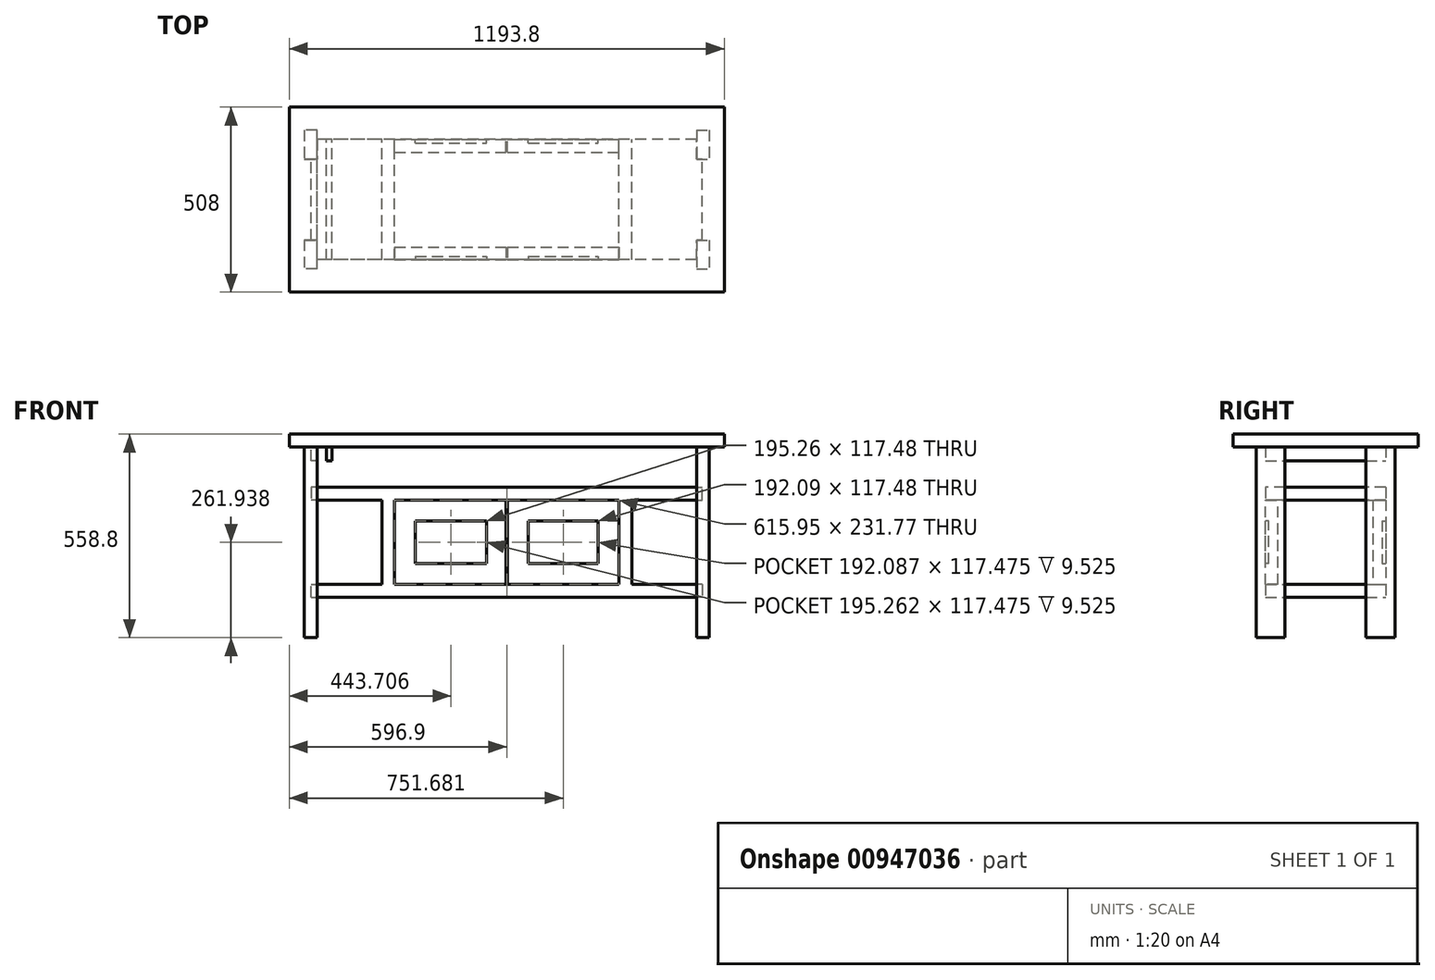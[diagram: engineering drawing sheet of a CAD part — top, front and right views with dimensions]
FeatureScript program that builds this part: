
annotation { "Feature Type Name" : "Feature", "Feature Type Description" : "" }
export const myFeature = defineFeature(function(context is Context, id is Id, definition is map)
    precondition{}
    {
        {
            var Q0;
            Q0=qCreatedBy(makeId("Front.planeOp"),FACE);
            var sketch = newSketch(context, id + "F0", { "sketchPlane" : qUnion([Q0])});
            skLineSegment(sketch, "E0.bottom", {"start": v(596.9, 558.8) * mm, "end": v(-596.9, 558.8) * mm});
            skLineSegment(sketch, "E0.top", {"start": v(596.9, 523.88) * mm, "end": v(-596.9, 523.88) * mm});
            skLineSegment(sketch, "E0.left", {"start": v(596.9, 558.8) * mm, "end": v(596.9, 523.88) * mm});
            skLineSegment(sketch, "E0.right", {"start": v(-596.9, 558.8) * mm, "end": v(-596.9, 523.88) * mm});
            skPoint(sketch, "E0.middle", {"position": v(0, 541.34) * mm});
            skLineSegment(sketch, "E1.bottom", {"start": v(536.58, 146.05) * mm, "end": v(342.9, 146.05) * mm});
            skLineSegment(sketch, "E1.top", {"start": v(536.58, 111.13) * mm, "end": v(-536.58, 111.12) * mm});
            skLineSegment(sketch, "E1.left", {"start": v(536.58, 146.05) * mm, "end": v(536.58, 111.13) * mm});
            skLineSegment(sketch, "E1.right", {"start": v(-536.58, 146.05) * mm, "end": v(-536.58, 111.12) * mm});
            skPoint(sketch, "E1.middle", {"position": v(0, 128.59) * mm});
            skLineSegment(sketch, "E2", {"start": v(307.98, 146.05) * mm, "end": v(307.98, 377.83) * mm});
            skLineSegment(sketch, "E3", {"start": v(342.9, 377.82) * mm, "end": v(342.9, 146.05) * mm});
            skLineSegment(sketch, "E4", {"start": v(0, 0) * mm, "end": v(0, -191.79) * mm, "construction": true});
            skLineSegment(sketch, "E5.MirrorCS", {"start": v(-342.9, 377.82) * mm, "end": v(-342.9, 146.05) * mm});
            skLineSegment(sketch, "E6.MirrorCS", {"start": v(-307.98, 146.05) * mm, "end": v(-307.98, 377.83) * mm});
            skLineSegment(sketch, "E7.trimOffspring", {"start": v(307.98, 146.05) * mm, "end": v(-307.98, 146.05) * mm});
            skLineSegment(sketch, "E8.trimOffspring", {"start": v(-342.9, 146.05) * mm, "end": v(-536.58, 146.05) * mm});
            skLineSegment(sketch, "E9.bottom", {"start": v(-536.58, 377.83) * mm, "end": v(-342.9, 377.83) * mm});
            skLineSegment(sketch, "E9.top", {"start": v(-536.58, 412.75) * mm, "end": v(536.57, 412.75) * mm});
            skLineSegment(sketch, "E9.left", {"start": v(-536.58, 377.83) * mm, "end": v(-536.58, 412.75) * mm});
            skLineSegment(sketch, "E9.right", {"start": v(536.58, 377.83) * mm, "end": v(536.58, 412.75) * mm});
            skLineSegment(sketch, "E10.trimOffspring", {"start": v(-307.98, 377.83) * mm, "end": v(307.97, 377.83) * mm});
            skLineSegment(sketch, "E11.trimOffspring", {"start": v(342.9, 377.83) * mm, "end": v(536.57, 377.83) * mm});
            skLineSegment(sketch, "E12", {"start": v(-342.9, 377.83) * mm, "end": v(-307.98, 377.83) * mm, "construction": true});
            skLineSegment(sketch, "E13.bottom", {"start": v(536.57, 523.88) * mm, "end": v(520.7, 523.88) * mm});
            skLineSegment(sketch, "E13.top", {"start": v(536.57, 485.78) * mm, "end": v(520.7, 485.78) * mm});
            skLineSegment(sketch, "E13.left", {"start": v(536.57, 523.88) * mm, "end": v(536.57, 485.78) * mm});
            skLineSegment(sketch, "E13.right", {"start": v(520.7, 523.88) * mm, "end": v(520.7, 485.78) * mm});
            skLineSegment(sketch, "E14.bottom", {"start": v(495.3, 523.88) * mm, "end": v(479.43, 523.88) * mm});
            skLineSegment(sketch, "E14.top", {"start": v(495.3, 485.78) * mm, "end": v(479.43, 485.78) * mm});
            skLineSegment(sketch, "E14.left", {"start": v(495.3, 523.88) * mm, "end": v(495.3, 485.78) * mm});
            skLineSegment(sketch, "E14.right", {"start": v(479.43, 523.88) * mm, "end": v(479.43, 485.78) * mm});
            skLineSegment(sketch, "E15.MirrorCS", {"start": v(-520.7, 523.88) * mm, "end": v(-520.7, 485.77) * mm});
            skLineSegment(sketch, "E16.MirrorCS", {"start": v(-495.3, 485.78) * mm, "end": v(-479.43, 485.78) * mm});
            skLineSegment(sketch, "E17.MirrorCS", {"start": v(-536.58, 485.77) * mm, "end": v(-520.7, 485.77) * mm});
            skLineSegment(sketch, "E18.MirrorCS", {"start": v(-495.3, 523.88) * mm, "end": v(-495.3, 485.77) * mm});
            skLineSegment(sketch, "E19.MirrorCS", {"start": v(-479.43, 523.88) * mm, "end": v(-479.43, 485.77) * mm});
            skLineSegment(sketch, "E20.MirrorCS", {"start": v(-536.57, 523.88) * mm, "end": v(-520.7, 523.88) * mm});
            skLineSegment(sketch, "E21.MirrorCS", {"start": v(-536.57, 523.88) * mm, "end": v(-536.57, 485.77) * mm});
            skLineSegment(sketch, "E22.MirrorCS", {"start": v(-495.3, 523.88) * mm, "end": v(-479.43, 523.88) * mm});
            skSolve(sketch);
        }
        {
            var Q0;
            Q0=makeQuery(id+"F0.imprint","IMPRINT",FACE,{"disambiguationData":[TD([[makeQuery(id+"F0.imprint","IMPRINT",EDGE,{"derivedFrom":sQuery(id+"F0.wireOp",EDGE,"E0.bottom")}),1.0]])]});
            extrude(context, id + "F1", {"entities" : qUnion([Q0]), "endBound" : BoundingType.SYMMETRIC, "depth" : 508 * mm, "offsetDistance" : 25.4 * mm});
        }
        {
            var Q0;
            Q0=makeQuery(id+"F0.imprint","IMPRINT",FACE,{"disambiguationData":[TD([[makeQuery(id+"F0.imprint","IMPRINT",EDGE,{"derivedFrom":sQuery(id+"F0.wireOp",EDGE,"E1.bottom")}),1.0]])]});
            var Q1;
            Q1=makeQuery(id+"F0.imprint","IMPRINT",FACE,{"disambiguationData":[TD([[makeQuery(id+"F0.imprint","IMPRINT",EDGE,{"derivedFrom":sQuery(id+"F0.wireOp",EDGE,"E13.bottom")}),1.0]])]});
            var Q2;
            Q2=makeQuery(id+"F0.imprint","IMPRINT",FACE,{"disambiguationData":[TD([[makeQuery(id+"F0.imprint","IMPRINT",EDGE,{"derivedFrom":sQuery(id+"F0.wireOp",EDGE,"E14.bottom")}),1.0]])]});
            var Q3;
            Q3=makeQuery(id+"F0.imprint","IMPRINT",FACE,{"disambiguationData":[TD([[makeQuery(id+"F0.imprint","IMPRINT",EDGE,{"derivedFrom":sQuery(id+"F0.wireOp",EDGE,"E16.MirrorCS")}),1.0]])]});
            var Q4;
            Q4=makeQuery(id+"F0.imprint","IMPRINT",FACE,{"disambiguationData":[TD([[makeQuery(id+"F0.imprint","IMPRINT",EDGE,{"derivedFrom":sQuery(id+"F0.wireOp",EDGE,"E15.MirrorCS")}),-1.0]])]});
            var Q5;
            Q5=makeQuery(id+"F1.opExtrude","CAP_FACE",FACE,{"disambiguationData":[OSD([sQuery(id+"F0.wireOp",EDGE,"E0.bottom"),sQuery(id+"F0.wireOp",EDGE,"E0.top"),sQuery(id+"F0.wireOp",EDGE,"E0.left"),sQuery(id+"F0.wireOp",EDGE,"E0.right"),sQuery(id+"F0.wireOp",EDGE,"VGV9EeQM-khb5-w9n3-FiPv-19kF0ZQjxZJE"),sQuery(id+"F0.wireOp",EDGE,"a7e9f2bc-2c81-4aa9-9757-ab29dbda99602.MirrorCS")])],"isStart":false});
            var Q6;
            Q6=makeQuery(id+"F1.opExtrude","CAP_FACE",FACE,{"disambiguationData":[OSD([sQuery(id+"F0.wireOp",EDGE,"E0.bottom"),sQuery(id+"F0.wireOp",EDGE,"E0.top"),sQuery(id+"F0.wireOp",EDGE,"E0.left"),sQuery(id+"F0.wireOp",EDGE,"E0.right"),sQuery(id+"F0.wireOp",EDGE,"VGV9EeQM-khb5-w9n3-FiPv-19kF0ZQjxZJE"),sQuery(id+"F0.wireOp",EDGE,"a7e9f2bc-2c81-4aa9-9757-ab29dbda99602.MirrorCS")])],"isStart":true});
            extrude(context, id + "F2", {"entities" : qUnion([Q0, Q1, Q2, Q3, Q4]), "endBound" : BoundingType.UP_TO_SURFACE, "depth" : 25.4 * mm, "endBoundEntityFace" : qUnion([Q5]), "hasOffset" : true, "offsetDistance" : 88.9 * mm, "hasSecondDirection" : true, "secondDirectionBound" : SecondDirectionBoundingType.UP_TO_SURFACE, "secondDirectionOppositeDirection" : true, "secondDirectionDepth" : 25.4 * mm, "secondDirectionBoundEntityFace" : qUnion([Q6]), "hasSecondDirectionOffset" : true, "secondDirectionOffsetDistance" : 88.9 * mm});
        }
        {
            var Q0;
            Q0=qCreatedBy(makeId("Top.planeOp"),FACE);
            var sketch = newSketch(context, id + "F3", { "sketchPlane" : qUnion([Q0])});
            skLineSegment(sketch, "E23", {"start": v(0, -153.77) * mm, "end": v(0, 0) * mm, "construction": true});
            skLineSegment(sketch, "E24.bottom", {"start": v(-555.63, 111.13) * mm, "end": v(-520.7, 111.13) * mm});
            skLineSegment(sketch, "E24.top", {"start": v(-555.63, 190.5) * mm, "end": v(-520.7, 190.5) * mm});
            skLineSegment(sketch, "E24.left", {"start": v(-555.62, 111.13) * mm, "end": v(-555.63, 190.5) * mm});
            skLineSegment(sketch, "E24.right", {"start": v(-520.7, 111.13) * mm, "end": v(-520.7, 190.5) * mm});
            skLineSegment(sketch, "E25.bottom", {"start": v(-555.63, -190.5) * mm, "end": v(-520.7, -190.5) * mm});
            skLineSegment(sketch, "E25.top", {"start": v(-555.63, -111.12) * mm, "end": v(-520.7, -111.12) * mm});
            skLineSegment(sketch, "E25.left", {"start": v(-555.62, -190.5) * mm, "end": v(-555.62, -111.12) * mm});
            skLineSegment(sketch, "E25.right", {"start": v(-520.7, -190.5) * mm, "end": v(-520.7, -111.13) * mm});
            skLineSegment(sketch, "E26.MirrorCS", {"start": v(520.7, -190.5) * mm, "end": v(520.7, -111.13) * mm});
            skLineSegment(sketch, "E27.MirrorCS", {"start": v(555.62, -190.5) * mm, "end": v(555.62, -111.13) * mm});
            skLineSegment(sketch, "E28.MirrorCS", {"start": v(555.63, 111.13) * mm, "end": v(520.7, 111.13) * mm});
            skLineSegment(sketch, "E29.MirrorCS", {"start": v(555.63, 190.5) * mm, "end": v(520.7, 190.5) * mm});
            skLineSegment(sketch, "E30.MirrorCS", {"start": v(555.62, 111.13) * mm, "end": v(555.62, 190.5) * mm});
            skLineSegment(sketch, "E31.MirrorCS", {"start": v(520.7, 111.13) * mm, "end": v(520.7, 190.5) * mm});
            skLineSegment(sketch, "E32.MirrorCS", {"start": v(555.62, -111.12) * mm, "end": v(520.7, -111.12) * mm});
            skLineSegment(sketch, "E33.MirrorCS", {"start": v(555.62, -190.5) * mm, "end": v(520.7, -190.5) * mm});
            skSolve(sketch);
        }
        {
            var Q0;
            Q0=qSketchRegion(id+"F3",true);
            var Q1;
            Q1=makeQuery(id+"F1.opExtrude","SWEPT_FACE",FACE,{"disambiguationData":[OSD([sQuery(id+"F0.wireOp",EDGE,"E0.top"),sQuery(id+"F0.wireOp",EDGE,"VGV9EeQM-khb5-w9n3-FiPv-19kF0ZQjxZJE"),sQuery(id+"F0.wireOp",EDGE,"a7e9f2bc-2c81-4aa9-9757-ab29dbda99602.MirrorCS")])]});
            extrude(context, id + "F4", {"entities" : qUnion([Q0]), "operationType" : NewBodyOperationType.ADD, "endBound" : BoundingType.UP_TO_SURFACE, "depth" : 25.4 * mm, "endBoundEntityFace" : qUnion([Q1]), "offsetDistance" : 25.4 * mm});
        }
        {
            var Q0;
            Q0=makeQuery(id+"F2.opExtrude","CAP_FACE",FACE,{"disambiguationData":[OSD([sQuery(id+"F0.wireOp",EDGE,"E0.bottom"),sQuery(id+"F0.wireOp",EDGE,"E0.top"),sQuery(id+"F0.wireOp",EDGE,"E0.left"),sQuery(id+"F0.wireOp",EDGE,"E0.right"),sQuery(id+"F0.wireOp",EDGE,"E9.top")])],"isStart":false});
            var sketch = newSketch(context, id + "F5", { "sketchPlane" : qUnion([Q0])});
            skLineSegment(sketch, "E34.bottom", {"start": v(-307.98, 377.83) * mm, "end": v(-1.59, 377.83) * mm});
            skLineSegment(sketch, "E34.top", {"start": v(-307.98, 146.05) * mm, "end": v(-1.59, 146.05) * mm});
            skLineSegment(sketch, "E34.left", {"start": v(-307.98, 377.83) * mm, "end": v(-307.98, 146.05) * mm});
            skLineSegment(sketch, "E34.right", {"start": v(-1.59, 377.83) * mm, "end": v(-1.59, 146.05) * mm});
            skLineSegment(sketch, "E35.bottom", {"start": v(1.59, 146.05) * mm, "end": v(307.98, 146.05) * mm});
            skLineSegment(sketch, "E35.top", {"start": v(1.59, 377.83) * mm, "end": v(307.98, 377.83) * mm});
            skLineSegment(sketch, "E35.left", {"start": v(1.59, 146.05) * mm, "end": v(1.59, 377.83) * mm});
            skLineSegment(sketch, "E35.right", {"start": v(307.98, 146.05) * mm, "end": v(307.98, 377.83) * mm});
            skLineSegment(sketch, "E36.0", {"start": v(-250.83, 320.68) * mm, "end": v(-55.56, 320.68) * mm});
            skLineSegment(sketch, "E36.1", {"start": v(-250.83, 320.68) * mm, "end": v(-250.83, 203.2) * mm});
            skLineSegment(sketch, "E36.2", {"start": v(-250.83, 203.2) * mm, "end": v(-55.56, 203.2) * mm});
            skLineSegment(sketch, "E36.3", {"start": v(-55.56, 203.2) * mm, "end": v(-55.56, 320.68) * mm});
            skLineSegment(sketch, "E37.0", {"start": v(58.74, 320.68) * mm, "end": v(250.83, 320.68) * mm});
            skLineSegment(sketch, "E37.1", {"start": v(58.74, 203.2) * mm, "end": v(58.74, 320.68) * mm});
            skLineSegment(sketch, "E37.2", {"start": v(58.74, 203.2) * mm, "end": v(250.82, 203.2) * mm});
            skLineSegment(sketch, "E37.3", {"start": v(250.83, 203.2) * mm, "end": v(250.83, 320.68) * mm});
            skPoint(sketch, "E38", {"position": v(-86.42, 145.11) * mm});
            skSolve(sketch);
        }
        {
            var Q0;
            Q0=qSketchRegion(id+"F5",true);
            var Q1;
            Q1=makeQuery(id+"F5.imprint","IMPRINT",FACE,{"disambiguationData":[TD([[makeQuery(id+"F5.imprint","IMPRINT",EDGE,{"derivedFrom":sQuery(id+"F5.wireOp",EDGE,"E36.0")}),-1.0]])]});
            var Q2;
            Q2=makeQuery(id+"F5.imprint","IMPRINT",FACE,{"disambiguationData":[TD([[makeQuery(id+"F5.imprint","IMPRINT",EDGE,{"derivedFrom":sQuery(id+"F5.wireOp",EDGE,"E37.0")}),-1.0]])]});
            extrude(context, id + "F6", {"entities" : qUnion([Q0, Q1, Q2]), "oppositeDirection" : true, "depth" : 34.92 * mm, "offsetDistance" : 25.4 * mm});
        }
        {
            var Q0;
            Q0=makeQuery(id+"F5.imprint","IMPRINT",FACE,{"disambiguationData":[TD([[makeQuery(id+"F5.imprint","IMPRINT",EDGE,{"derivedFrom":sQuery(id+"F5.wireOp",EDGE,"E36.0")}),-1.0]])]});
            var Q1;
            Q1=makeQuery(id+"F5.imprint","IMPRINT",FACE,{"disambiguationData":[TD([[makeQuery(id+"F5.imprint","IMPRINT",EDGE,{"derivedFrom":sQuery(id+"F5.wireOp",EDGE,"E37.0")}),-1.0]])]});
            extrude(context, id + "F7", {"entities" : qUnion([Q0, Q1]), "operationType" : NewBodyOperationType.REMOVE, "oppositeDirection" : true, "depth" : 9.52 * mm, "offsetDistance" : 25.4 * mm});
        }
        {
            var Q0;
            Q0=makeQuery(id+"F6.opExtrude","SWEPT_BODY",BODY,{"disambiguationData":[OSD([sQuery(id+"F5.wireOp",EDGE,"E34.bottom"),sQuery(id+"F5.wireOp",EDGE,"E34.top"),sQuery(id+"F5.wireOp",EDGE,"E34.left"),sQuery(id+"F5.wireOp",EDGE,"E34.right")])]});
            var Q1;
            Q1=makeQuery(id+"F6.opExtrude","SWEPT_BODY",BODY,{"disambiguationData":[OSD([sQuery(id+"F5.wireOp",EDGE,"E35.bottom"),sQuery(id+"F5.wireOp",EDGE,"E35.top"),sQuery(id+"F5.wireOp",EDGE,"E35.left"),sQuery(id+"F5.wireOp",EDGE,"E35.right")])]});
            var Q2;
            Q2=qCreatedBy(makeId("Front.planeOp"),FACE);
            mirror(context, id + "F8", {"entities" : qUnion([Q0, Q1]), "mirrorPlane" : qUnion([Q2])});
        }
    });
